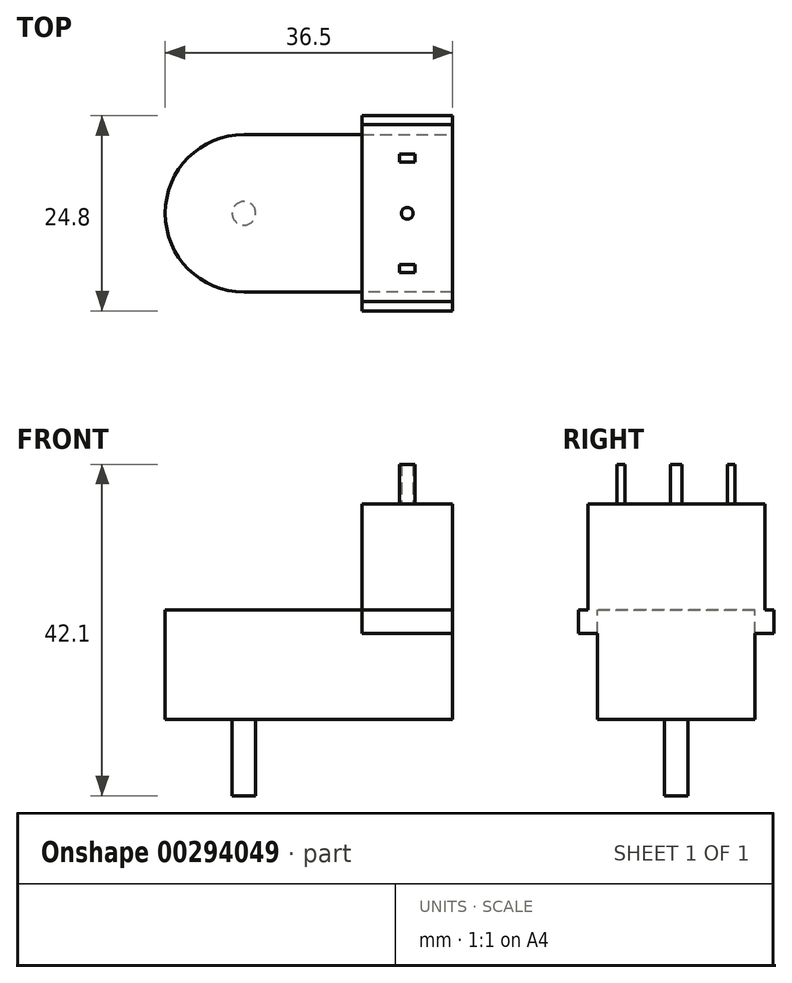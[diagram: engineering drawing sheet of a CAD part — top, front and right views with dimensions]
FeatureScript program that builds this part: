
annotation { "Feature Type Name" : "Feature", "Feature Type Description" : "" }
export const myFeature = defineFeature(function(context is Context, id is Id, definition is map)
    precondition{}
    {
        {
            var Q0;
            Q0=qCreatedBy(makeId("Top.planeOp"),FACE);
            var sketch = newSketch(context, id + "F0", { "sketchPlane" : qUnion([Q0])});
            skArc(sketch, "E0", {"start": v(0, 10) * mm, "mid": v(-10, 0) * mm, "end": v(0, -10) * mm});
            skLineSegment(sketch, "E1", {"start": v(0, 10) * mm, "end": v(26.5, 10) * mm});
            skLineSegment(sketch, "E2", {"start": v(26.5, 10) * mm, "end": v(26.5, -10) * mm});
            skLineSegment(sketch, "E3", {"start": v(26.5, -10) * mm, "end": v(0, -10) * mm});
            skSolve(sketch);
        }
        {
            var Q0;
            Q0=makeQuery(id+"F0.imprint","IMPRINT",FACE,{"disambiguationData":[TD([[makeQuery(id+"F0.imprint","IMPRINT",EDGE,{"derivedFrom":sQuery(id+"F0.wireOp",EDGE,"E0")}),1.0]])]});
            extrude(context, id + "F1", {"entities" : qUnion([Q0]), "depth" : (27.4 - 13.5) * mm});
        }
        {
            var Q0;
            Q0=makeQuery(id+"F1.opExtrude","CAP_FACE",FACE,{"disambiguationData":[OSD([sQuery(id+"F0.wireOp",EDGE,"E0"),sQuery(id+"F0.wireOp",EDGE,"E1"),sQuery(id+"F0.wireOp",EDGE,"E2"),sQuery(id+"F0.wireOp",EDGE,"E3")])],"isStart":true});
            var sketch = newSketch(context, id + "F2", { "sketchPlane" : qUnion([Q0])});
            skCircle(sketch, "E4", {"center": v(0, 0) * mm, "radius": 1.5 * mm});
            skSolve(sketch);
        }
        {
            var Q0;
            Q0 = qSketchRegion(id + "F2", true);
            extrude(context, id + "F3", {"entities" : qUnion([Q0]), "operationType" : NewBodyOperationType.ADD, "depth" : 9.7 * mm});
        }
        {
            var Q0;
            Q0=makeQuery(id+"F1.opExtrude","CAP_FACE",FACE,{"disambiguationData":[OSD([sQuery(id+"F0.wireOp",EDGE,"E0"),sQuery(id+"F0.wireOp",EDGE,"E1"),sQuery(id+"F0.wireOp",EDGE,"E2"),sQuery(id+"F0.wireOp",EDGE,"E3")])],"isStart":false});
            var sketch = newSketch(context, id + "F4", { "sketchPlane" : qUnion([Q0])});
            skPoint(sketch, "E5.0", {"position": v(26.5, 10) * mm});
            skLineSegment(sketch, "E6", {"start": v(0, 0) * mm, "end": v(38.4, 0) * mm, "construction": true});
            skLineSegment(sketch, "E7.bottom", {"start": v(26.5, 10) * mm, "end": v(15, 10) * mm});
            skLineSegment(sketch, "E7.top", {"start": v(26.5, 12.4) * mm, "end": v(15, 12.4) * mm});
            skLineSegment(sketch, "E7.left", {"start": v(26.5, 10) * mm, "end": v(26.5, 12.4) * mm});
            skLineSegment(sketch, "E7.right", {"start": v(15, 10) * mm, "end": v(15, 12.4) * mm});
            skLineSegment(sketch, "E8.MirrorCS", {"start": v(26.5, -10) * mm, "end": v(26.5, -12.4) * mm});
            skLineSegment(sketch, "E9.MirrorCS", {"start": v(26.5, -12.4) * mm, "end": v(15, -12.4) * mm});
            skLineSegment(sketch, "E10.MirrorCS", {"start": v(15, -10) * mm, "end": v(15, -12.4) * mm});
            skLineSegment(sketch, "E11.MirrorCS", {"start": v(26.5, -10) * mm, "end": v(15, -10) * mm});
            skSolve(sketch);
        }
        {
            var Q0;
            Q0 = qSketchRegion(id + "F4", true);
            extrude(context, id + "F5", {"entities" : qUnion([Q0]), "operationType" : NewBodyOperationType.ADD, "oppositeDirection" : true, "depth" : 3 * mm});
        }
        {
            var Q0;
            Q0=makeQuery(id+"F5.boolean.opBoolean","MERGE",FACE,{"derivedFrom":[makeQuery(id+"F1.opExtrude","CAP_FACE",FACE,{"disambiguationData":[OSD([sQuery(id+"F0.wireOp",EDGE,"E0"),sQuery(id+"F0.wireOp",EDGE,"E1"),sQuery(id+"F0.wireOp",EDGE,"E2"),sQuery(id+"F0.wireOp",EDGE,"E3")])],"isStart":false}),makeQuery(id+"F5.opExtrude","CAP_FACE",FACE,{"disambiguationData":[OSD([sQuery(id+"F4.wireOp",EDGE,"E7.bottom"),sQuery(id+"F4.wireOp",EDGE,"E7.top"),sQuery(id+"F4.wireOp",EDGE,"E7.left"),sQuery(id+"F4.wireOp",EDGE,"E7.right")])],"isStart":true}),makeQuery(id+"F5.opExtrude","CAP_FACE",FACE,{"disambiguationData":[OSD([sQuery(id+"F4.wireOp",EDGE,"E8.MirrorCS"),sQuery(id+"F4.wireOp",EDGE,"E9.MirrorCS"),sQuery(id+"F4.wireOp",EDGE,"E10.MirrorCS"),sQuery(id+"F4.wireOp",EDGE,"E11.MirrorCS")])],"isStart":true})]});
            var sketch = newSketch(context, id + "F6", { "sketchPlane" : qUnion([Q0])});
            skLineSegment(sketch, "E12.bottom", {"start": v(26.5, 11.3) * mm, "end": v(15, 11.3) * mm});
            skLineSegment(sketch, "E12.top", {"start": v(26.5, -11.2) * mm, "end": v(15, -11.2) * mm});
            skLineSegment(sketch, "E12.left", {"start": v(26.5, 11.3) * mm, "end": v(26.5, -11.2) * mm});
            skLineSegment(sketch, "E12.right", {"start": v(15, 11.3) * mm, "end": v(15, -11.2) * mm});
            skLineSegment(sketch, "E13", {"start": v(15, 0) * mm, "end": v(0, 0) * mm, "construction": true});
            skSolve(sketch);
        }
        {
            var Q0;
            Q0 = qSketchRegion(id + "F6", true);
            extrude(context, id + "F7", {"entities" : qUnion([Q0]), "operationType" : NewBodyOperationType.ADD, "depth" : 13.5 * mm});
        }
        {
            var Q0;
            Q0=makeQuery(id+"F7.opExtrude","CAP_FACE",FACE,{"disambiguationData":[OSD([sQuery(id+"F6.wireOp",EDGE,"E12.bottom"),sQuery(id+"F6.wireOp",EDGE,"E12.top"),sQuery(id+"F6.wireOp",EDGE,"E12.left"),sQuery(id+"F6.wireOp",EDGE,"E12.right")])],"isStart":false});
            var sketch = newSketch(context, id + "F8", { "sketchPlane" : qUnion([Q0])});
            skCircle(sketch, "E14", {"center": v(20.75, 0) * mm, "radius": 0.75 * mm});
            skLineSegment(sketch, "E15", {"start": v(20.75, 0) * mm, "end": v(20.75, 11.3) * mm, "construction": true});
            skLineSegment(sketch, "E16", {"start": v(0, 0) * mm, "end": v(20.75, 0) * mm, "construction": true});
            skLineSegment(sketch, "E17.bottom", {"start": v(19.75, 7.5) * mm, "end": v(21.75, 7.5) * mm});
            skLineSegment(sketch, "E17.top", {"start": v(19.75, 6.5) * mm, "end": v(21.75, 6.5) * mm});
            skLineSegment(sketch, "E17.left", {"start": v(19.75, 7.5) * mm, "end": v(19.75, 6.5) * mm});
            skLineSegment(sketch, "E17.right", {"start": v(21.75, 7.5) * mm, "end": v(21.75, 6.5) * mm});
            skPoint(sketch, "E17.middle", {"position": v(20.75, 7) * mm});
            skLineSegment(sketch, "E18.MirrorCS", {"start": v(21.75, -7.5) * mm, "end": v(21.75, -6.5) * mm});
            skLineSegment(sketch, "E19.MirrorCS", {"start": v(19.75, -7.5) * mm, "end": v(19.75, -6.5) * mm});
            skLineSegment(sketch, "E20.MirrorCS", {"start": v(19.75, -6.5) * mm, "end": v(21.75, -6.5) * mm});
            skLineSegment(sketch, "E21.MirrorCS", {"start": v(19.75, -7.5) * mm, "end": v(21.75, -7.5) * mm});
            skPoint(sketch, "E22.MirrorP", {"position": v(20.75, -7) * mm});
            skSolve(sketch);
        }
        {
            var Q0;
            Q0 = qSketchRegion(id + "F8", true);
            extrude(context, id + "F9", {"entities" : qUnion([Q0]), "operationType" : NewBodyOperationType.ADD, "depth" : 5 * mm});
        }
    });
